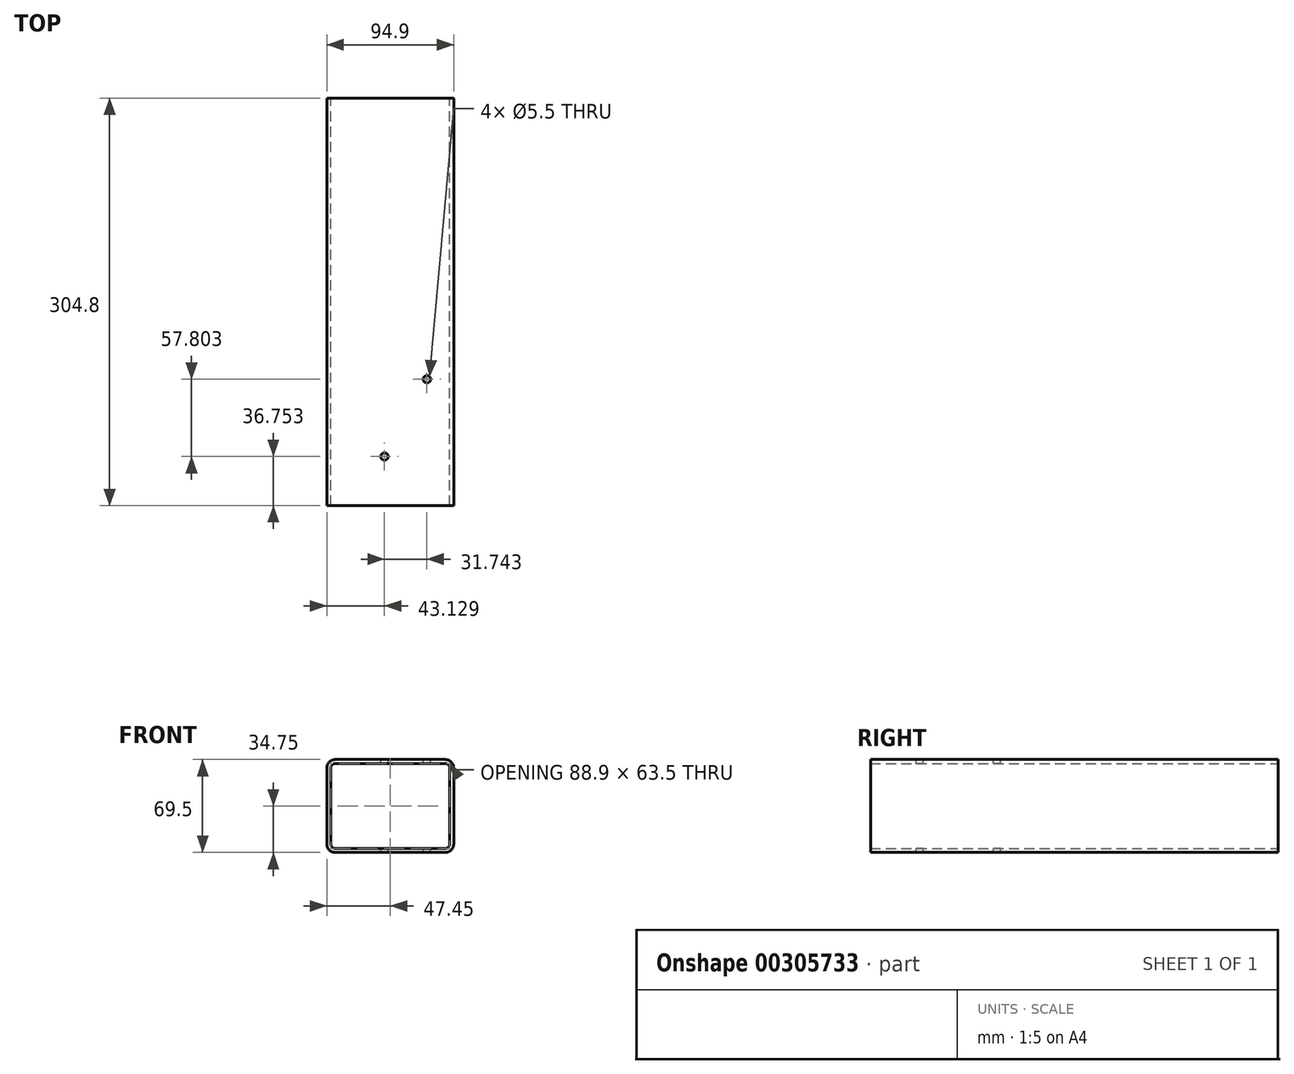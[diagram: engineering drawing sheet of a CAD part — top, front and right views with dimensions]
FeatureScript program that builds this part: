
annotation { "Feature Type Name" : "Feature", "Feature Type Description" : "" }
export const myFeature = defineFeature(function(context is Context, id is Id, definition is map)
    precondition{}
    {
        {
            var Q0;
            Q0=qCreatedBy(makeId("Front.planeOp"),FACE);
            var sketch = newSketch(context, id + "F0", { "sketchPlane" : qUnion([Q0])});
            skLineSegment(sketch, "E0.bottom", {"start": v(-41.28, 31.75) * mm, "end": v(41.28, 31.75) * mm});
            skLineSegment(sketch, "E0.top", {"start": v(-41.28, -31.75) * mm, "end": v(41.27, -31.75) * mm});
            skLineSegment(sketch, "E0.left", {"start": v(-44.45, 28.58) * mm, "end": v(-44.45, -28.57) * mm});
            skLineSegment(sketch, "E0.right", {"start": v(44.45, 28.58) * mm, "end": v(44.45, -28.57) * mm});
            skPoint(sketch, "E0.middle", {"position": v(0, 0) * mm});
            skPoint(sketch, "E1.visualSharp", {"position": v(-44.45, 31.75) * mm});
            skArc(sketch, "E1.filletArc", {"start": v(-41.28, 31.75) * mm, "mid": v(-43.52, 30.82) * mm, "end": v(-44.45, 28.58) * mm});
            skPoint(sketch, "E2.visualSharp", {"position": v(-44.45, -31.75) * mm});
            skArc(sketch, "E2.filletArc", {"start": v(-44.45, -28.57) * mm, "mid": v(-43.52, -30.82) * mm, "end": v(-41.28, -31.75) * mm});
            skPoint(sketch, "E3.visualSharp", {"position": v(44.45, -31.75) * mm});
            skArc(sketch, "E3.filletArc", {"start": v(41.27, -31.75) * mm, "mid": v(43.52, -30.82) * mm, "end": v(44.45, -28.57) * mm});
            skPoint(sketch, "E4.visualSharp", {"position": v(44.45, 31.75) * mm});
            skArc(sketch, "E4.filletArc", {"start": v(44.45, 28.58) * mm, "mid": v(43.52, 30.82) * mm, "end": v(41.28, 31.75) * mm});
            skLineSegment(sketch, "E5.0", {"start": v(-41.28, 34.75) * mm, "end": v(41.28, 34.75) * mm});
            skArc(sketch, "E5.1", {"start": v(47.45, 28.58) * mm, "mid": v(45.64, 32.94) * mm, "end": v(41.28, 34.75) * mm});
            skArc(sketch, "E5.2", {"start": v(-41.28, 34.75) * mm, "mid": v(-45.64, 32.94) * mm, "end": v(-47.45, 28.58) * mm});
            skLineSegment(sketch, "E5.3", {"start": v(47.45, 28.58) * mm, "end": v(47.45, -28.57) * mm});
            skLineSegment(sketch, "E5.4", {"start": v(-47.45, 28.58) * mm, "end": v(-47.45, -28.57) * mm});
            skArc(sketch, "E5.5", {"start": v(-47.45, -28.57) * mm, "mid": v(-45.64, -32.94) * mm, "end": v(-41.28, -34.75) * mm});
            skLineSegment(sketch, "E5.6", {"start": v(-41.28, -34.75) * mm, "end": v(41.27, -34.75) * mm});
            skArc(sketch, "E5.7", {"start": v(41.27, -34.75) * mm, "mid": v(45.64, -32.94) * mm, "end": v(47.45, -28.57) * mm});
            skSolve(sketch);
        }
        {
            var Q0;
            Q0=makeQuery(id+"F0.imprint","IMPRINT",FACE,{"disambiguationData":[TD([[makeQuery(id+"F0.imprint","IMPRINT",EDGE,{"derivedFrom":sQuery(id+"F0.wireOp",EDGE,"E0.bottom")}),1.0]])]});
            extrude(context, id + "F1", {"entities" : qUnion([Q0]), "endBound" : BoundingType.SYMMETRIC, "depth" : 304.8 * mm});
        }
        {
            var Q0;
            Q0=makeQuery(id+"F1.opExtrude","SWEPT_FACE",FACE,{"disambiguationData":[OSD([sQuery(id+"F0.wireOp",EDGE,"E5.0")])]});
            var sketch = newSketch(context, id + "F2", { "sketchPlane" : qUnion([Q0])});
            skPoint(sketch, "E6", {"position": v(-4.32, -115.65) * mm});
            skPoint(sketch, "E7", {"position": v(27.42, -57.84) * mm});
            skSolve(sketch);
        }
        {
            var Q0;
            Q0=sQuery(id+"F2.wireOp",VERTEX,"E7");
            var Q1;
            Q1=sQuery(id+"F2.wireOp",VERTEX,"E6");
            var Q2;
            Q2=makeQuery(id+"F1.opExtrude","SWEPT_BODY",BODY,{"disambiguationData":[OSD([sQuery(id+"F0.wireOp",EDGE,"E0.bottom"),sQuery(id+"F0.wireOp",EDGE,"E0.top"),sQuery(id+"F0.wireOp",EDGE,"E0.left"),sQuery(id+"F0.wireOp",EDGE,"E0.right"),sQuery(id+"F0.wireOp",EDGE,"E1.filletArc"),sQuery(id+"F0.wireOp",EDGE,"E2.filletArc"),sQuery(id+"F0.wireOp",EDGE,"E3.filletArc"),sQuery(id+"F0.wireOp",EDGE,"E4.filletArc"),sQuery(id+"F0.wireOp",EDGE,"E5.0"),sQuery(id+"F0.wireOp",EDGE,"E5.1"),sQuery(id+"F0.wireOp",EDGE,"E5.2"),sQuery(id+"F0.wireOp",EDGE,"E5.3"),sQuery(id+"F0.wireOp",EDGE,"E5.4"),sQuery(id+"F0.wireOp",EDGE,"E5.5"),sQuery(id+"F0.wireOp",EDGE,"E5.6"),sQuery(id+"F0.wireOp",EDGE,"E5.7")])]});
            hole(context, id + "F3", {"style" : HoleStyle.SIMPLE, "endStyle" : HoleEndStyle.THROUGH, "standardTappedOrClearance" : lookupTablePath({ "standard" : "ISO", "fit" : "Normal", "size" : "M5", "type" : "Clearance" }), "standardBlindInLast" : lookupTablePath({ "fit" : "Standard", "standard" : "ISO", "size" : "M5", "type" : "Clearance" }), "holeDiameter" : 5.5 * mm, "tappedDepth" : 12.7 * mm, "tapClearance" : 3, "locations" : qUnion([Q0, Q1]), "scope" : qUnion([Q2])});
        }
    });
